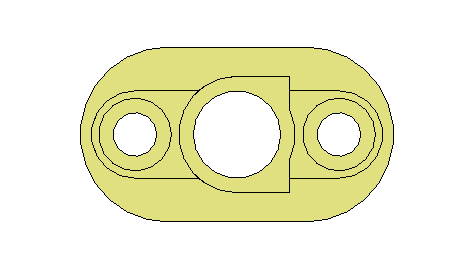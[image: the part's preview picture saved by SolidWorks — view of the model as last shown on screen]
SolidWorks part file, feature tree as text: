
SOLIDWORKS PART (.sldprt)
format: sldprt  version: not decoded by parser v0  size: 172,032 bytes
history: native  units: mm
features: plane x3, extrude x3, cut_extrude x3, sketch x2, material x1 + 6 further entries (+7 scaffold rows collapsed)
feature tree (25):
  scaffold x7  (default folders/planes/origin — collapsed)
  material  "Matériau <non spécifié>"
  "Corps de surface"
  plane  "Face"
  plane  "Dessus"
  plane  "Droite"
  sketch  "Esquisse1"
  sketch  "param"  dims[D1=19.0mm D2=24.0mm]
  extrude  "Extrusion1"  Depth=2mm
  "Esquisse2"
  extrude  "Extrusion4"  Depth=2mm
  "Esquisse4"
  extrude  "Extrusion5"  Depth=4mm
  "Esquisse3"
  cut_extrude  "Enlèv. mat.-Extru.1"  Depth=10mm
  "Esquisse5"
  cut_extrude  "Enlèv. mat.-Extru.2"  [1 undecoded]
  "Esquisse6"
  cut_extrude  "Enlèv. mat.-Extru.3"  Depth=2mm
decode coverage: 6 of 8 modeling features carry decoded parameters; 6 rows unclassified (native names shown)
note: 1 parameter value undecoded
note: suppression state not decoded; provenance and decode notes live in map.json
